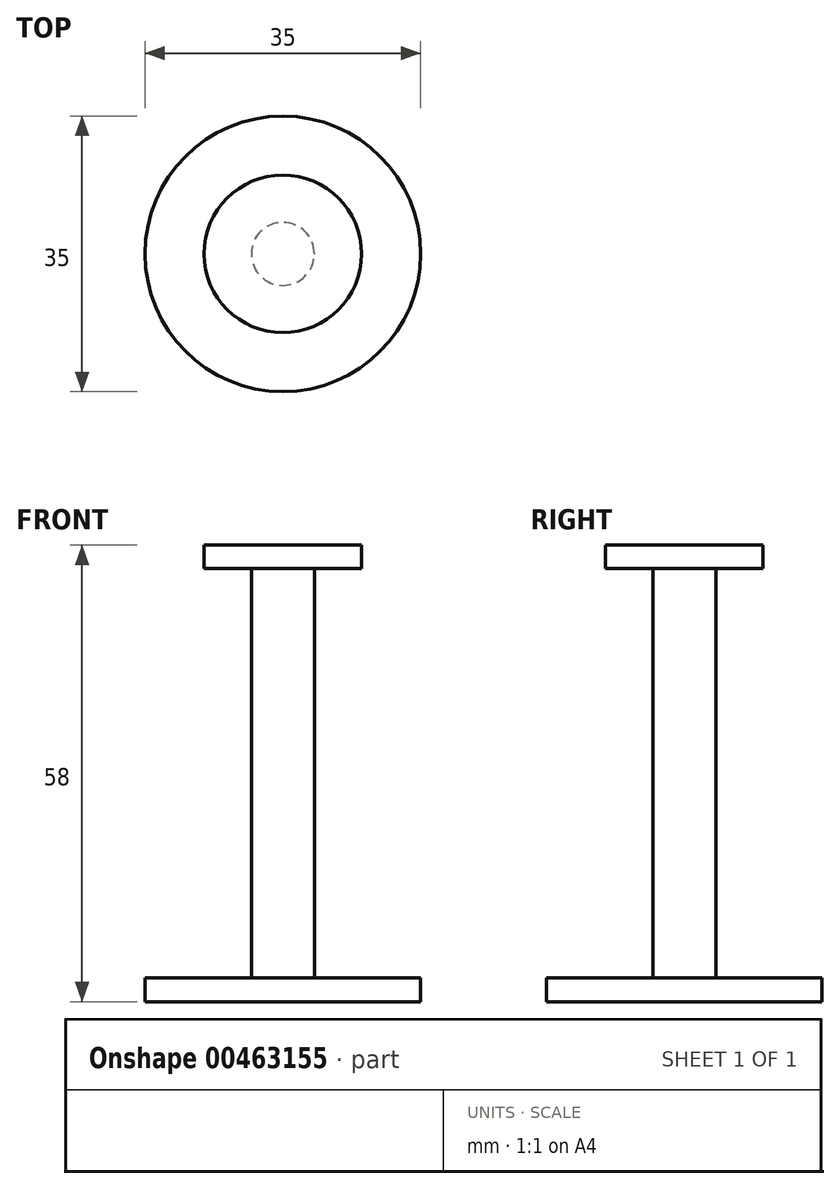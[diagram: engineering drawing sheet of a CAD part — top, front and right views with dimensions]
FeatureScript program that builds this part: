
annotation { "Feature Type Name" : "Feature", "Feature Type Description" : "" }
export const myFeature = defineFeature(function(context is Context, id is Id, definition is map)
    precondition{}
    {
        {
            var Q0;
            Q0=qCreatedBy(makeId("Top.planeOp"),FACE);
            var sketch = newSketch(context, id + "F0", { "sketchPlane" : qUnion([Q0])});
            skCircle(sketch, "E0", {"center": v(0, 0) * mm, "radius": 4 * mm});
            skCircle(sketch, "E1", {"center": v(0, 0) * mm, "radius": 17.5 * mm});
            skSolve(sketch);
        }
        {
            var Q0;
            Q0=makeQuery(id+"F0.imprint","IMPRINT",FACE,{"disambiguationData":[TD([[makeQuery(id+"F0.imprint","IMPRINT",EDGE,{"derivedFrom":sQuery(id+"F0.wireOp",EDGE,"E0")}),-1.0]])]});
            var Q1;
            Q1=makeQuery(id+"F0.imprint","IMPRINT",FACE,{"disambiguationData":[TD([[makeQuery(id+"F0.imprint","IMPRINT",EDGE,{"derivedFrom":sQuery(id+"F0.wireOp",EDGE,"E0")}),1.0]])]});
            extrude(context, id + "F1", {"entities" : qUnion([Q0, Q1]), "depth" : 3 * mm});
        }
        {
            var Q0;
            Q0=makeQuery(id+"F0.imprint","IMPRINT",FACE,{"disambiguationData":[TD([[makeQuery(id+"F0.imprint","IMPRINT",EDGE,{"derivedFrom":sQuery(id+"F0.wireOp",EDGE,"E0")}),1.0]])]});
            extrude(context, id + "F2", {"entities" : qUnion([Q0]), "operationType" : NewBodyOperationType.ADD, "depth" : 55 * mm});
        }
        {
            var Q0;
            Q0=makeQuery(id+"F2.opExtrude","CAP_FACE",FACE,{"disambiguationData":[OSD([sQuery(id+"F0.wireOp",EDGE,"E0")])],"isStart":false});
            var sketch = newSketch(context, id + "F3", { "sketchPlane" : qUnion([Q0])});
            skCircle(sketch, "E2", {"center": v(0, 0) * mm, "radius": 10 * mm});
            skSolve(sketch);
        }
        {
            var Q0;
            Q0=makeQuery(id+"F3.imprint","IMPRINT",FACE,{"disambiguationData":[TD([[makeQuery(id+"F3.imprint","IMPRINT",EDGE,{"derivedFrom":sQuery(id+"F3.wireOp",EDGE,"E2")}),1.0]])]});
            var Q1;
            Q1=makeQuery(id+"F3.imprint","IMPRINT",FACE,{"disambiguationData":[TD([[makeQuery(id+"F3.imprint","IMPRINT",EDGE,{"derivedFrom":makeQuery(id+"F2.opExtrude","CAP_EDGE",EDGE,{"disambiguationData":[OSD([sQuery(id+"F0.wireOp",EDGE,"E0")])],"isStart":false})}),1.0]])]});
            extrude(context, id + "F4", {"entities" : qUnion([Q0, Q1]), "operationType" : NewBodyOperationType.ADD, "depth" : 3 * mm});
        }
    });
